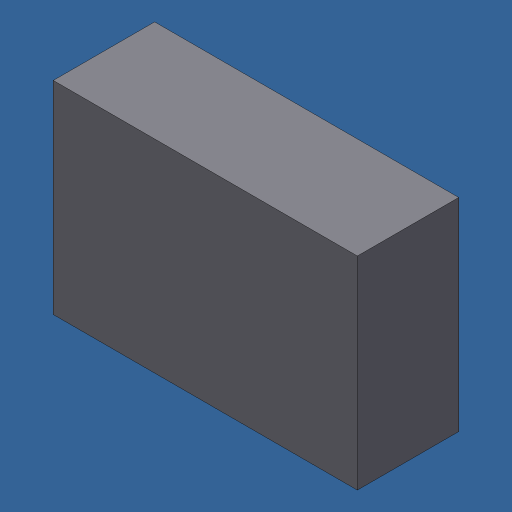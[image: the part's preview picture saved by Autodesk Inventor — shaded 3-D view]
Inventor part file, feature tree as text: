
AUTODESK INVENTOR PART (.ipt)
format: ipt  version: 2024.3 (Build 283343000, 343)  size: 109,056 bytes
history: native  units: mm (DEFAULTED — no unit token found)
features: other x1, extrude x1
ambient origin geometry x8: Origin, YZ Plane, XZ Plane, XY Plane, X Axis, Y Axis, Z Axis, Center Point
bodies: Body1 (feature_tree)
feature tree (2):
  other  "Finish - None"
  extrude  "Extrusion1"  TaperAngle=0.0deg  [1 undecoded]
note: 1 required parameter value undecoded (feature->parameter linkage not recoverable at this tier; creation-order binding heuristic only, values carry confidence <= 0.55)
